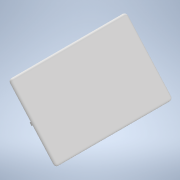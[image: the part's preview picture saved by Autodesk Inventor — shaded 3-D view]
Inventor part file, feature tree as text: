
AUTODESK INVENTOR PART (.ipt)
format: ipt  version: 2022 (Build 260153000, 153)  size: 231,424 bytes
history: native  units: mm
features: other x5, extrude x3, fillet x3, sketch x3, reference x1
ambient origin geometry x8: Origin, YZ Plane, XZ Plane, XY Plane, X Axis, Y Axis, Z Axis, Center Point
bodies: Body1 (feature_tree)
feature tree (15):
  other  "Твердое тело1"
  other  "РабПлоскость1"
  extrude  "Выдавливание1"  Depth=12.0mm
  extrude  "Выдавливание2"  Depth=12.0mm
  extrude  "Выдавливание3"  Depth=16.0mm
  fillet  "Сопряжение1"  Radius=57.902002mm
  fillet  "Сопряжение2"  Radius=6.0mm
  fillet  "Сопряжение3"  Radius=100.0mm
  sketch  "Эскиз1"
  reference  "Ссылка1"
  sketch  "Эскиз2"
  sketch  "Эскиз3"
  other  "<userpath>\Documents\Inventor\AIM\Aim.iam"
  other  "Aim.iam"
  other  "Fastener:1"
